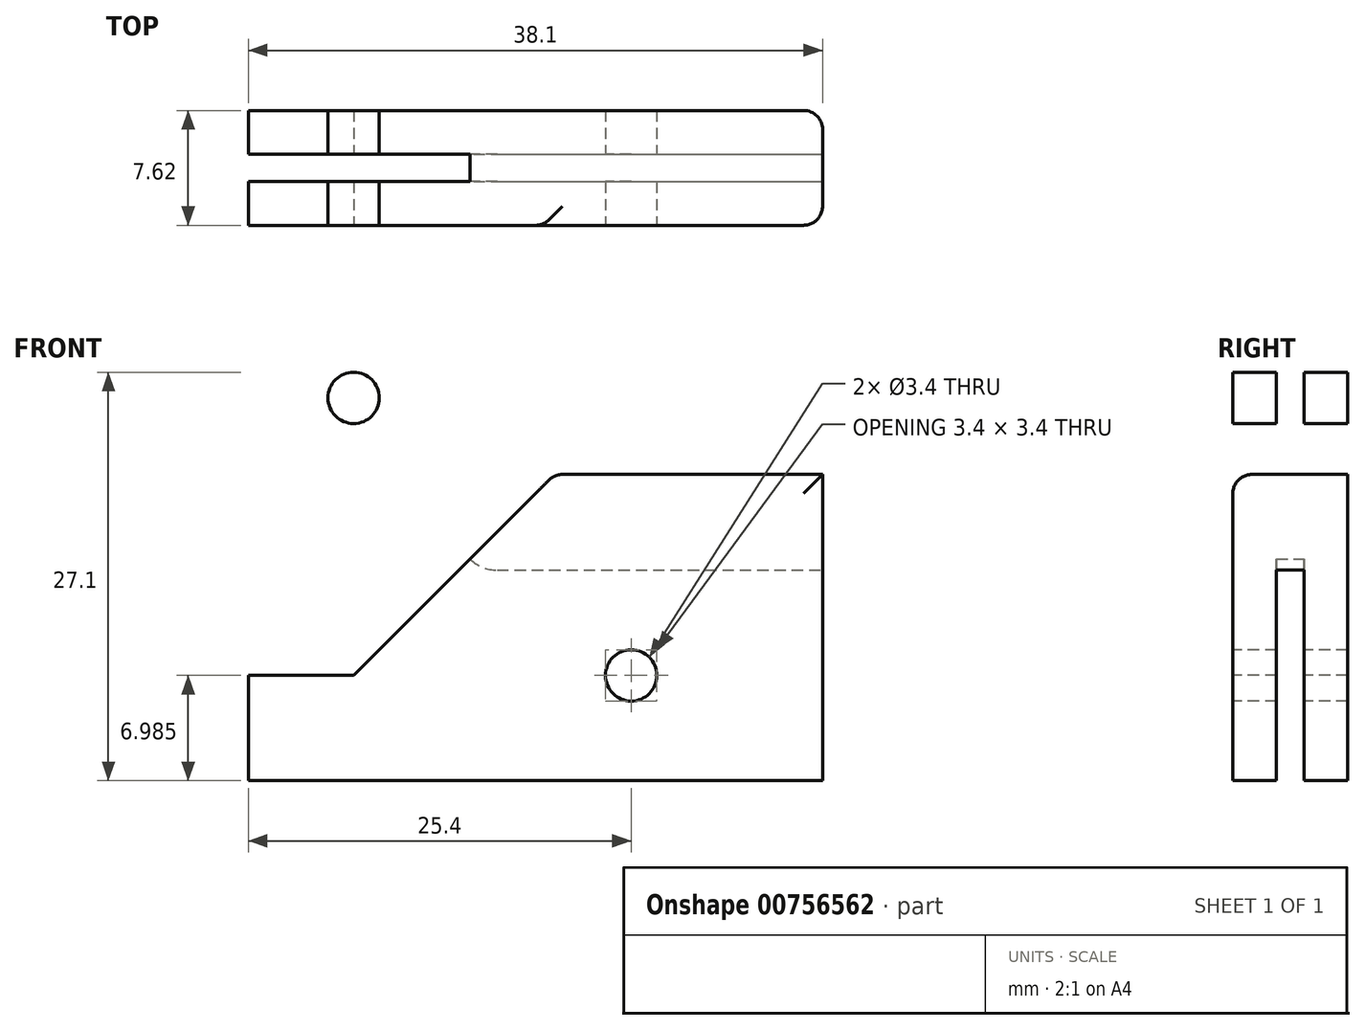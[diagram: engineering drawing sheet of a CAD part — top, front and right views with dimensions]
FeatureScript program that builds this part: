
annotation { "Feature Type Name" : "Feature", "Feature Type Description" : "" }
export const myFeature = defineFeature(function(context is Context, id is Id, definition is map)
    precondition{}
    {
        {
            var Q0;
            Q0=qCreatedBy(makeId("Front.planeOp"),FACE);
            var sketch = newSketch(context, id + "F0", { "sketchPlane" : qUnion([Q0])});
            skLineSegment(sketch, "E0.bottom", {"start": v(0, 0) * mm, "end": v(38.1, 0) * mm});
            skLineSegment(sketch, "E0.top", {"start": v(0, 38.1) * mm, "end": v(38.1, 38.1) * mm});
            skLineSegment(sketch, "E0.left", {"start": v(0, 0) * mm, "end": v(0, 38.1) * mm});
            skLineSegment(sketch, "E0.right", {"start": v(38.1, 0) * mm, "end": v(38.1, 38.1) * mm});
            skSolve(sketch);
        }
        {
            var Q0;
            Q0 = qSketchRegion(id + "F0", true);
            extrude(context, id + "F1", {"entities" : qUnion([Q0]), "depth" : 7.62 * mm, "offsetDistance" : 25.4 * mm});
        }
        {
            var Q0;
            Q0=makeQuery(id+"F1.opExtrude","SWEPT_FACE",FACE,{"disambiguationData":[OSD([sQuery(id+"F0.wireOp",EDGE,"E0.right")])]});
            var sketch = newSketch(context, id + "F2", { "sketchPlane" : qUnion([Q0])});
            skLineSegment(sketch, "E1.bottom", {"start": v(-4.72, 0) * mm, "end": v(-2.9, 0) * mm});
            skLineSegment(sketch, "E1.top", {"start": v(-4.72, 13.97) * mm, "end": v(-2.9, 13.97) * mm});
            skLineSegment(sketch, "E1.left", {"start": v(-4.72, 0) * mm, "end": v(-4.72, 13.97) * mm});
            skLineSegment(sketch, "E1.right", {"start": v(-2.9, 0) * mm, "end": v(-2.9, 13.97) * mm});
            skLineSegment(sketch, "E2", {"start": v(-4.72, 13.97) * mm, "end": v(-7.62, 13.97) * mm});
            skLineSegment(sketch, "E3", {"start": v(-2.9, 13.97) * mm, "end": v(0, 13.97) * mm});
            skSolve(sketch);
        }
        {
            var Q0;
            Q0 = qSketchRegion(id + "F2", true);
            extrude(context, id + "F3", {"entities" : qUnion([Q0]), "operationType" : NewBodyOperationType.REMOVE, "endBound" : BoundingType.THROUGH_ALL, "oppositeDirection" : true, "depth" : 25.4 * mm, "offsetDistance" : 25.4 * mm});
        }
        {
            var Q0;
            Q0=makeQuery(id+"F1.opExtrude","SWEPT_FACE",FACE,{"disambiguationData":[OSD([sQuery(id+"F0.wireOp",EDGE,"E0.top")])]});
            var sketch = newSketch(context, id + "F4", { "sketchPlane" : qUnion([Q0])});
            skLineSegment(sketch, "E4.bottom", {"start": v(0, -2.9) * mm, "end": v(13.97, -2.9) * mm});
            skLineSegment(sketch, "E4.top", {"start": v(0, -4.72) * mm, "end": v(13.97, -4.72) * mm});
            skLineSegment(sketch, "E4.left", {"start": v(0, -2.9) * mm, "end": v(0, -4.72) * mm});
            skLineSegment(sketch, "E4.right", {"start": v(13.97, -2.9) * mm, "end": v(13.97, -4.72) * mm});
            skLineSegment(sketch, "E5", {"start": v(13.97, -2.9) * mm, "end": v(13.97, 0) * mm});
            skLineSegment(sketch, "E6", {"start": v(13.97, -4.72) * mm, "end": v(13.97, -7.62) * mm});
            skSolve(sketch);
        }
        {
            var Q0;
            Q0 = qSketchRegion(id + "F4", true);
            extrude(context, id + "F5", {"entities" : qUnion([Q0]), "operationType" : NewBodyOperationType.REMOVE, "endBound" : BoundingType.THROUGH_ALL, "oppositeDirection" : true, "depth" : 25.4 * mm, "offsetDistance" : 25.4 * mm});
        }
        {
            var Q0;
            Q0=makeQuery(id+"F1.opExtrude","CAP_FACE",FACE,{"disambiguationData":[OSD([sQuery(id+"F0.wireOp",EDGE,"E0.bottom"),sQuery(id+"F0.wireOp",EDGE,"E0.top"),sQuery(id+"F0.wireOp",EDGE,"E0.left"),sQuery(id+"F0.wireOp",EDGE,"E0.right")])],"isStart":true});
            var sketch = newSketch(context, id + "F6", { "sketchPlane" : qUnion([Q0])});
            skLineSegment(sketch, "E7.bottom", {"start": v(-38.1, 38.1) * mm, "end": v(-20.32, 38.1) * mm});
            skLineSegment(sketch, "E7.top", {"start": v(-38.1, 20.32) * mm, "end": v(-20.32, 20.32) * mm});
            skLineSegment(sketch, "E7.left", {"start": v(-38.1, 38.1) * mm, "end": v(-38.1, 20.32) * mm});
            skLineSegment(sketch, "E7.right", {"start": v(-20.32, 38.1) * mm, "end": v(-20.32, 20.32) * mm});
            skSolve(sketch);
        }
        {
            var Q0;
            Q0 = qSketchRegion(id + "F6", true);
            extrude(context, id + "F7", {"entities" : qUnion([Q0]), "operationType" : NewBodyOperationType.REMOVE, "endBound" : BoundingType.THROUGH_ALL, "oppositeDirection" : true, "depth" : 25.4 * mm, "offsetDistance" : 25.4 * mm});
        }
        {
            var Q0;
            Q0=makeQuery(id+"F5.boolean.opBoolean","INTERSECT",EDGE,{"derivedFrom":[makeQuery(id+"F3.boolean.opBoolean","COPY",FACE,{"derivedFrom":makeQuery(id+"F3.opExtrude","SWEPT_FACE",FACE,{"disambiguationData":[OSD([sQuery(id+"F2.wireOp",EDGE,"E1.top")])]})}),makeQuery(id+"F5.opExtrude","SWEPT_FACE",FACE,{"disambiguationData":[OSD([sQuery(id+"F4.wireOp",EDGE,"E4.right")])]})]});
            fillet(context, id + "F8", {"entities" : qUnion([Q0]), "radius" : 2.54 * mm, "tangentPropagation" : true, "allowEdgeOverflow" : false});
        }
        {
            var Q0;
            Q0=makeQuery(id+"F1.opExtrude","CAP_FACE",FACE,{"disambiguationData":[OSD([sQuery(id+"F0.wireOp",EDGE,"E0.bottom"),sQuery(id+"F0.wireOp",EDGE,"E0.top"),sQuery(id+"F0.wireOp",EDGE,"E0.left"),sQuery(id+"F0.wireOp",EDGE,"E0.right")])],"isStart":false});
            var sketch = newSketch(context, id + "F9", { "sketchPlane" : qUnion([Q0])});
            skLineSegment(sketch, "E8.bottom", {"start": v(0, 0) * mm, "end": v(25.4, 0) * mm});
            skLineSegment(sketch, "E8.top", {"start": v(0, 6.99) * mm, "end": v(25.4, 6.99) * mm});
            skLineSegment(sketch, "E8.left", {"start": v(0, 0) * mm, "end": v(0, 6.99) * mm});
            skLineSegment(sketch, "E8.right", {"start": v(25.4, 0) * mm, "end": v(25.4, 6.99) * mm});
            skCircle(sketch, "E9", {"center": v(25.4, 6.99) * mm, "radius": 1.7 * mm});
            skLineSegment(sketch, "E10", {"start": v(0, 0) * mm, "end": v(21.5, 21.5) * mm});
            skCircle(sketch, "E11.MirrorC", {"center": v(6.98, 25.4) * mm, "radius": 1.7 * mm});
            skSolve(sketch);
        }
        {
            var Q0;
            Q0=makeQuery(id+"F9.imprint","IMPRINT",FACE,{"disambiguationData":[TD([[makeQuery(id+"F9.imprint","IMPRINT",EDGE,{"derivedFrom":sQuery(id+"F9.wireOp",EDGE,"E11.MirrorC")}),-1.0]])]});
            var Q1;
            {var subQ0=sQuery(id+"F9.wireOp",EDGE,"E8.right");var subQ1=sQuery(id+"F9.wireOp",EDGE,"E8.top");var subQ2=makeQuery(id+"F9.imprint","INTERSECT",VERTEX,{"derivedFrom":[subQ1,subQ0]});Q1=makeQuery(id+"F9.imprint","IMPRINT",FACE,{"disambiguationData":[TD([[makeQuery(id+"F9.imprint","IMPRINT",EDGE,{"disambiguationData":[TD([[subQ2,1.0]])],"derivedFrom":subQ1}),-1.0]])]});}
            var Q2;
            {var subQ0=sQuery(id+"F9.wireOp",EDGE,"E8.right");var subQ1=sQuery(id+"F9.wireOp",EDGE,"E8.top");var subQ2=makeQuery(id+"F9.imprint","INTERSECT",VERTEX,{"derivedFrom":[subQ1,subQ0]});Q2=makeQuery(id+"F9.imprint","IMPRINT",FACE,{"disambiguationData":[TD([[makeQuery(id+"F9.imprint","IMPRINT",EDGE,{"disambiguationData":[TD([[subQ2,1.0]])],"derivedFrom":subQ1}),1.0]])]});}
            extrude(context, id + "F10", {"entities" : qUnion([Q0, Q1, Q2]), "operationType" : NewBodyOperationType.REMOVE, "endBound" : BoundingType.THROUGH_ALL, "oppositeDirection" : true, "depth" : 25.4 * mm, "offsetDistance" : 25.4 * mm});
        }
        {
            var Q0;
            Q0=makeQuery(id+"F1.opExtrude","CAP_EDGE",EDGE,{"disambiguationData":[OSD([sQuery(id+"F0.wireOp",EDGE,"E0.top")])],"isStart":true});
            var Q1;
            Q1=makeQuery(id+"F1.opExtrude","CAP_EDGE",EDGE,{"disambiguationData":[OSD([sQuery(id+"F0.wireOp",EDGE,"E0.top")])],"isStart":false});
            var Q2;
            Q2=makeQuery(id+"F7.boolean.opBoolean","COPY",EDGE,{"derivedFrom":makeQuery(id+"F7.opExtrude","SWEPT_EDGE",EDGE,{"disambiguationData":[OSD([sQuery(id+"F0.wireOp",EDGE,"E0.top"),sQuery(id+"F6.wireOp",EDGE,"E7.bottom"),sQuery(id+"F6.wireOp",EDGE,"E7.right")])]})});
            var Q3;
            Q3=makeQuery(id+"F7.boolean.opBoolean","COPY",EDGE,{"derivedFrom":makeQuery(id+"F7.opExtrude","CAP_EDGE",EDGE,{"disambiguationData":[OSD([sQuery(id+"F6.wireOp",EDGE,"E7.right")])],"isStart":true})});
            var Q4;
            Q4=makeQuery(id+"F7.boolean.opBoolean","INTERSECT",EDGE,{"derivedFrom":[makeQuery(id+"F1.opExtrude","CAP_FACE",FACE,{"disambiguationData":[OSD([sQuery(id+"F0.wireOp",EDGE,"E0.bottom"),sQuery(id+"F0.wireOp",EDGE,"E0.top"),sQuery(id+"F0.wireOp",EDGE,"E0.left"),sQuery(id+"F0.wireOp",EDGE,"E0.right")])],"isStart":false}),makeQuery(id+"F7.opExtrude","SWEPT_FACE",FACE,{"disambiguationData":[OSD([sQuery(id+"F6.wireOp",EDGE,"E7.right")])]})]});
            var Q5;
            Q5=makeQuery(id+"F7.boolean.opBoolean","COPY",EDGE,{"derivedFrom":makeQuery(id+"F7.opExtrude","SWEPT_EDGE",EDGE,{"disambiguationData":[OSD([sQuery(id+"F6.wireOp",EDGE,"E7.top"),sQuery(id+"F6.wireOp",EDGE,"E7.right")])]})});
            var Q6;
            Q6=makeQuery(id+"F7.boolean.opBoolean","COPY",EDGE,{"derivedFrom":makeQuery(id+"F7.opExtrude","SWEPT_EDGE",EDGE,{"disambiguationData":[OSD([sQuery(id+"F0.wireOp",EDGE,"E0.right"),sQuery(id+"F6.wireOp",EDGE,"E7.top"),sQuery(id+"F6.wireOp",EDGE,"E7.left")])]})});
            var Q7;
            Q7=makeQuery(id+"F7.boolean.opBoolean","COPY",EDGE,{"derivedFrom":makeQuery(id+"F7.opExtrude","CAP_EDGE",EDGE,{"disambiguationData":[OSD([sQuery(id+"F6.wireOp",EDGE,"E7.top")])],"isStart":true})});
            var Q8;
            Q8=makeQuery(id+"F7.boolean.opBoolean","INTERSECT",EDGE,{"derivedFrom":[makeQuery(id+"F1.opExtrude","CAP_FACE",FACE,{"disambiguationData":[OSD([sQuery(id+"F0.wireOp",EDGE,"E0.bottom"),sQuery(id+"F0.wireOp",EDGE,"E0.top"),sQuery(id+"F0.wireOp",EDGE,"E0.left"),sQuery(id+"F0.wireOp",EDGE,"E0.right")])],"isStart":false}),makeQuery(id+"F7.opExtrude","SWEPT_FACE",FACE,{"disambiguationData":[OSD([sQuery(id+"F6.wireOp",EDGE,"E7.top")])]})]});
            var Q9;
            Q9=makeQuery(id+"F1.opExtrude","CAP_EDGE",EDGE,{"disambiguationData":[OSD([sQuery(id+"F0.wireOp",EDGE,"E0.right")])],"isStart":true});
            var Q10;
            Q10=makeQuery(id+"F1.opExtrude","CAP_EDGE",EDGE,{"disambiguationData":[OSD([sQuery(id+"F0.wireOp",EDGE,"E0.right")])],"isStart":false});
            fillet(context, id + "F11", {"entities" : qUnion([Q0, Q1, Q2, Q3, Q4, Q5, Q6, Q7, Q8, Q9, Q10]), "radius" : 1.27 * mm, "tangentPropagation" : true, "allowEdgeOverflow" : false});
        }
    });
